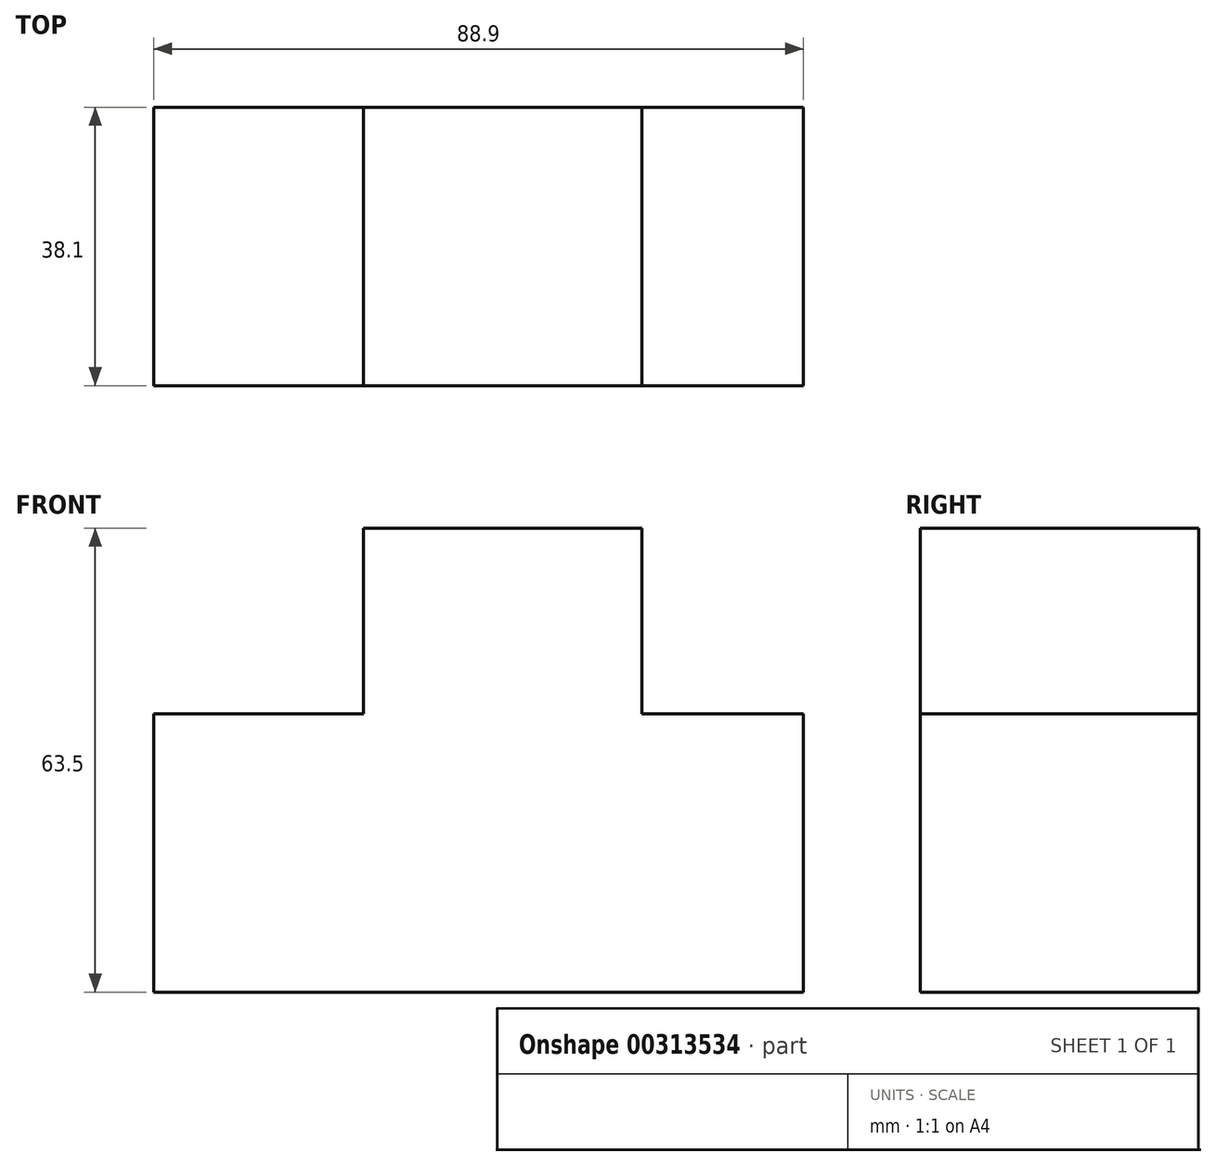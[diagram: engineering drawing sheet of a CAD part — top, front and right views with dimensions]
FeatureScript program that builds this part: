
annotation { "Feature Type Name" : "Feature", "Feature Type Description" : "" }
export const myFeature = defineFeature(function(context is Context, id is Id, definition is map)
    precondition{}
    {
        {
            var Q0;
            Q0=qCreatedBy(makeId("Front.planeOp"),FACE);
            var sketch = newSketch(context, id + "F0", { "sketchPlane" : qUnion([Q0])});
            skLineSegment(sketch, "E0", {"start": v(-45.55, -39.36) * mm, "end": v(43.35, -39.36) * mm});
            skLineSegment(sketch, "E1", {"start": v(43.35, -39.36) * mm, "end": v(43.35, -1.26) * mm});
            skLineSegment(sketch, "E2", {"start": v(43.35, -1.26) * mm, "end": v(21.24, -1.26) * mm});
            skLineSegment(sketch, "E3", {"start": v(21.24, -1.26) * mm, "end": v(21.24, 24.14) * mm});
            skLineSegment(sketch, "E4", {"start": v(21.24, 24.14) * mm, "end": v(-16.86, 24.14) * mm});
            skLineSegment(sketch, "E5", {"start": v(-16.86, 24.14) * mm, "end": v(-16.86, -1.26) * mm});
            skLineSegment(sketch, "E6", {"start": v(-16.86, -1.26) * mm, "end": v(-45.55, -1.26) * mm});
            skLineSegment(sketch, "E7", {"start": v(-45.55, -1.26) * mm, "end": v(-45.55, -39.36) * mm});
            skSolve(sketch);
        }
        {
            var Q0;
            Q0=makeQuery(id+"F0.imprint","IMPRINT",FACE,{"disambiguationData":[TD([[makeQuery(id+"F0.imprint","IMPRINT",EDGE,{"derivedFrom":sQuery(id+"F0.wireOp",EDGE,"E0")}),1.0]])]});
            extrude(context, id + "F1", {"entities" : qUnion([Q0]), "depth" : 38.1 * mm});
        }
    });
